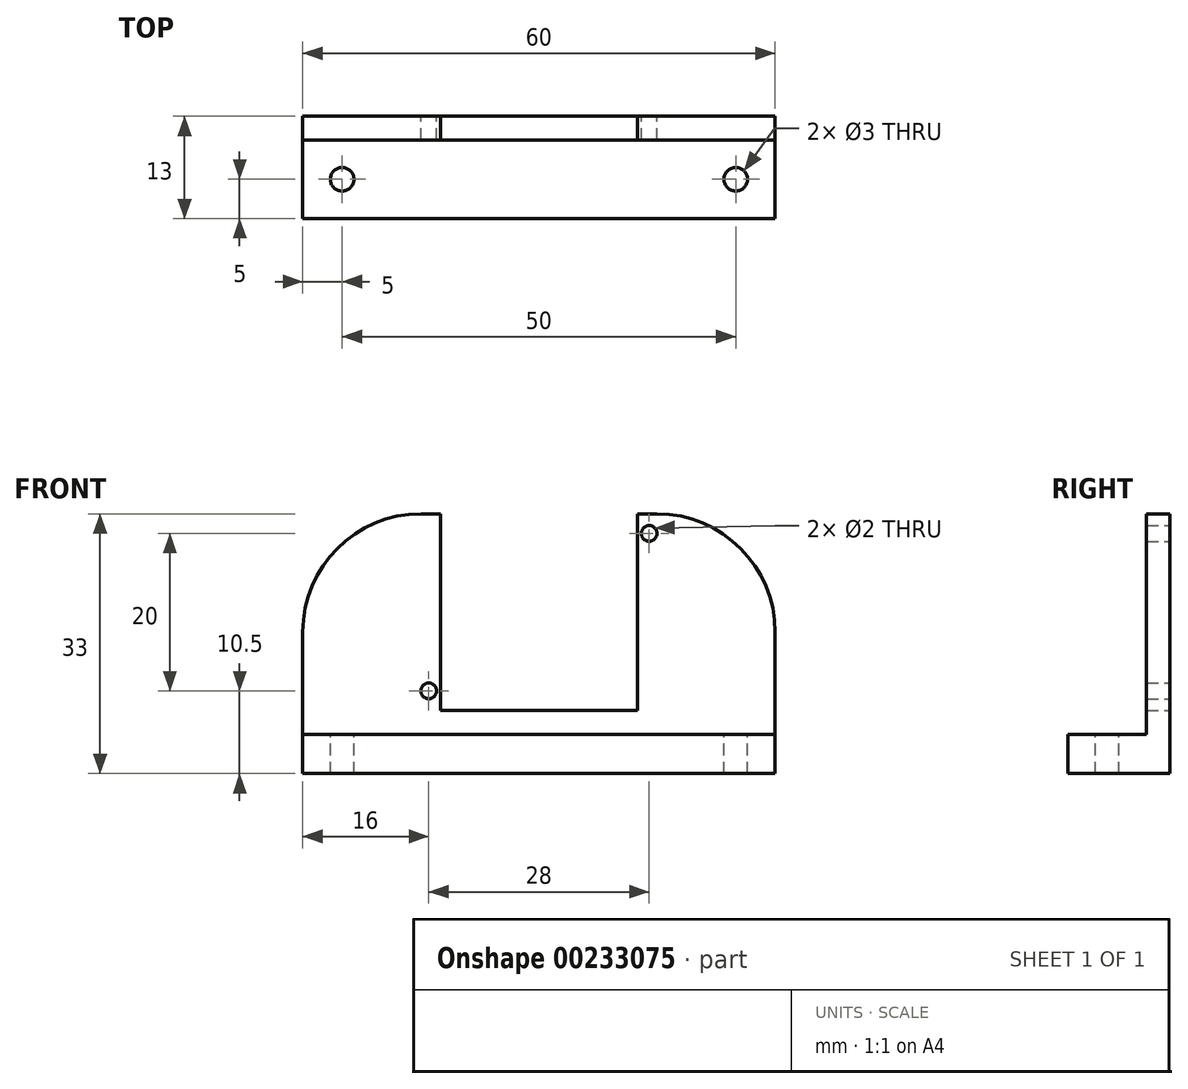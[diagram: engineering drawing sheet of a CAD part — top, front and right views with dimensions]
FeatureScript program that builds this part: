
annotation { "Feature Type Name" : "Feature", "Feature Type Description" : "" }
export const myFeature = defineFeature(function(context is Context, id is Id, definition is map)
    precondition{}
    {
        {
            var Q0;
            Q0=qCreatedBy(makeId("Top.planeOp"),FACE);
            var sketch = newSketch(context, id + "F0", { "sketchPlane" : qUnion([Q0])});
            skLineSegment(sketch, "E0.bottom", {"start": v(0, 0) * mm, "end": v(60, 0) * mm});
            skLineSegment(sketch, "E0.top", {"start": v(0, 13) * mm, "end": v(60, 13) * mm});
            skLineSegment(sketch, "E0.left", {"start": v(0, 0) * mm, "end": v(0, 13) * mm});
            skLineSegment(sketch, "E0.right", {"start": v(60, 0) * mm, "end": v(60, 13) * mm});
            skSolve(sketch);
        }
        {
            var Q0;
            Q0=makeQuery(id+"F0.imprint","IMPRINT",FACE,{"disambiguationData":[TD([[makeQuery(id+"F0.imprint","IMPRINT",EDGE,{"derivedFrom":sQuery(id+"F0.wireOp",EDGE,"E0.bottom")}),1.0]])]});
            extrude(context, id + "F1", {"entities" : qUnion([Q0]), "depth" : 5 * mm});
        }
        {
            var Q0;
            Q0=makeQuery(id+"F1.opExtrude","CAP_FACE",FACE,{"disambiguationData":[OSD([sQuery(id+"F0.wireOp",EDGE,"E0.bottom"),sQuery(id+"F0.wireOp",EDGE,"E0.top"),sQuery(id+"F0.wireOp",EDGE,"E0.left"),sQuery(id+"F0.wireOp",EDGE,"E0.right")])],"isStart":false});
            var sketch = newSketch(context, id + "F2", { "sketchPlane" : qUnion([Q0])});
            skLineSegment(sketch, "E1", {"start": v(5, 5) * mm, "end": v(55, 5) * mm});
            skPoint(sketch, "E2", {"position": v(30, 5) * mm});
            skPoint(sketch, "E3", {"position": v(30, 0) * mm});
            skPoint(sketch, "E4", {"position": v(60, 5) * mm});
            skSolve(sketch);
        }
        {
            var Q0;
            Q0=sQuery(id+"F2.wireOp",VERTEX,"E1.start");
            var Q1;
            Q1=sQuery(id+"F2.wireOp",VERTEX,"E1.end");
            var Q2;
            Q2=makeQuery(id+"F1.opExtrude","SWEPT_BODY",BODY,{"disambiguationData":[OSD([sQuery(id+"F0.wireOp",EDGE,"E0.bottom"),sQuery(id+"F0.wireOp",EDGE,"E0.top"),sQuery(id+"F0.wireOp",EDGE,"E0.left"),sQuery(id+"F0.wireOp",EDGE,"E0.right")])]});
            hole(context, id + "F3", {"style" : HoleStyle.SIMPLE, "endStyle" : HoleEndStyle.THROUGH, "holeDiameter" : 3 * mm, "locations" : qUnion([Q0, Q1]), "scope" : qUnion([Q2]), "isTappedThrough" : true});
        }
        {
            var Q0;
            Q0=makeQuery(id+"F1.opExtrude","CAP_FACE",FACE,{"disambiguationData":[OSD([sQuery(id+"F0.wireOp",EDGE,"E0.bottom"),sQuery(id+"F0.wireOp",EDGE,"E0.top"),sQuery(id+"F0.wireOp",EDGE,"E0.left"),sQuery(id+"F0.wireOp",EDGE,"E0.right")])],"isStart":false});
            var sketch = newSketch(context, id + "F4", { "sketchPlane" : qUnion([Q0])});
            skLineSegment(sketch, "E5.bottom", {"start": v(0, 13) * mm, "end": v(60, 13) * mm});
            skLineSegment(sketch, "E5.top", {"start": v(0, 10) * mm, "end": v(60, 10) * mm});
            skLineSegment(sketch, "E5.left", {"start": v(0, 13) * mm, "end": v(0, 10) * mm});
            skLineSegment(sketch, "E5.right", {"start": v(60, 13) * mm, "end": v(60, 10) * mm});
            skSolve(sketch);
        }
        {
            var Q0;
            Q0=makeQuery(id+"F4.imprint","IMPRINT",FACE,{"disambiguationData":[TD([[makeQuery(id+"F4.imprint","IMPRINT",EDGE,{"derivedFrom":sQuery(id+"F4.wireOp",EDGE,"E5.bottom")}),-1.0]])]});
            extrude(context, id + "F5", {"entities" : qUnion([Q0]), "operationType" : NewBodyOperationType.ADD, "depth" : 28 * mm});
        }
        {
            var Q0;
            Q0=makeQuery(id+"F5.boolean.opBoolean","MERGE",FACE,{"derivedFrom":[makeQuery(id+"F1.opExtrude","SWEPT_FACE",FACE,{"disambiguationData":[OSD([sQuery(id+"F0.wireOp",EDGE,"E0.top")])]}),makeQuery(id+"F5.opExtrude","SWEPT_FACE",FACE,{"disambiguationData":[OSD([sQuery(id+"F4.wireOp",EDGE,"E5.bottom")])]})]});
            var sketch = newSketch(context, id + "F6", { "sketchPlane" : qUnion([Q0])});
            skLineSegment(sketch, "E6.bottom", {"start": v(-42.5, 33) * mm, "end": v(-17.5, 33) * mm});
            skLineSegment(sketch, "E6.top", {"start": v(-42.5, 8) * mm, "end": v(-17.5, 8) * mm});
            skLineSegment(sketch, "E6.left", {"start": v(-42.5, 33) * mm, "end": v(-42.5, 8) * mm});
            skLineSegment(sketch, "E6.right", {"start": v(-17.5, 33) * mm, "end": v(-17.5, 8) * mm});
            skPoint(sketch, "E7", {"position": v(-30, 0) * mm});
            skPoint(sketch, "E8", {"position": v(-30, 8) * mm});
            skSolve(sketch);
        }
        {
            var Q0;
            Q0=makeQuery(id+"F6.imprint","IMPRINT",FACE,{"disambiguationData":[TD([[makeQuery(id+"F6.imprint","IMPRINT",EDGE,{"derivedFrom":sQuery(id+"F6.wireOp",EDGE,"E6.bottom")}),1.0]])]});
            extrude(context, id + "F7", {"entities" : qUnion([Q0]), "operationType" : NewBodyOperationType.REMOVE, "oppositeDirection" : true, "depth" : 5 * mm});
        }
        {
            var Q0;
            Q0=makeQuery(id+"F5.boolean.opBoolean","MERGE",FACE,{"derivedFrom":[makeQuery(id+"F1.opExtrude","SWEPT_FACE",FACE,{"disambiguationData":[OSD([sQuery(id+"F0.wireOp",EDGE,"E0.top")])]}),makeQuery(id+"F5.opExtrude","SWEPT_FACE",FACE,{"disambiguationData":[OSD([sQuery(id+"F4.wireOp",EDGE,"E5.bottom")])]})]});
            var sketch = newSketch(context, id + "F8", { "sketchPlane" : qUnion([Q0])});
            skPoint(sketch, "E9", {"position": v(-44, 30.5) * mm});
            skPoint(sketch, "E10", {"position": v(-16, 10.5) * mm});
            skLineSegment(sketch, "E11", {"start": v(-44, 30.5) * mm, "end": v(-16, 30.5) * mm, "construction": true});
            skLineSegment(sketch, "E12", {"start": v(-44, 30.5) * mm, "end": v(-44, 10.5) * mm, "construction": true});
            skPoint(sketch, "E13", {"position": v(-44, 20.5) * mm});
            skPoint(sketch, "E14", {"position": v(-42.5, 20.5) * mm});
            skPoint(sketch, "E15", {"position": v(-30, 8) * mm});
            skPoint(sketch, "E16", {"position": v(-30, 30.5) * mm});
            skSolve(sketch);
        }
        {
            var Q0;
            Q0=sQuery(id+"F8.wireOp",VERTEX,"E9");
            var Q1;
            Q1=sQuery(id+"F8.wireOp",VERTEX,"E10");
            var Q2;
            Q2=makeQuery(id+"F1.opExtrude","SWEPT_BODY",BODY,{"disambiguationData":[OSD([sQuery(id+"F0.wireOp",EDGE,"E0.bottom"),sQuery(id+"F0.wireOp",EDGE,"E0.top"),sQuery(id+"F0.wireOp",EDGE,"E0.left"),sQuery(id+"F0.wireOp",EDGE,"E0.right")])]});
            hole(context, id + "F9", {"style" : HoleStyle.SIMPLE, "endStyle" : HoleEndStyle.THROUGH, "holeDiameter" : 2 * mm, "locations" : qUnion([Q0, Q1]), "scope" : qUnion([Q2]), "isTappedThrough" : true});
        }
        {
            var Q0;
            Q0=makeQuery(id+"F5.opExtrude","CAP_EDGE",EDGE,{"disambiguationData":[OSD([sQuery(id+"F4.wireOp",EDGE,"E5.left")])],"isStart":false});
            var Q1;
            Q1=makeQuery(id+"F5.opExtrude","CAP_EDGE",EDGE,{"disambiguationData":[OSD([sQuery(id+"F4.wireOp",EDGE,"E5.right")])],"isStart":false});
            fillet(context, id + "F10", {"entities" : qUnion([Q0, Q1]), "radius" : 15 * mm, "tangentPropagation" : true, "allowEdgeOverflow" : false});
        }
    });
